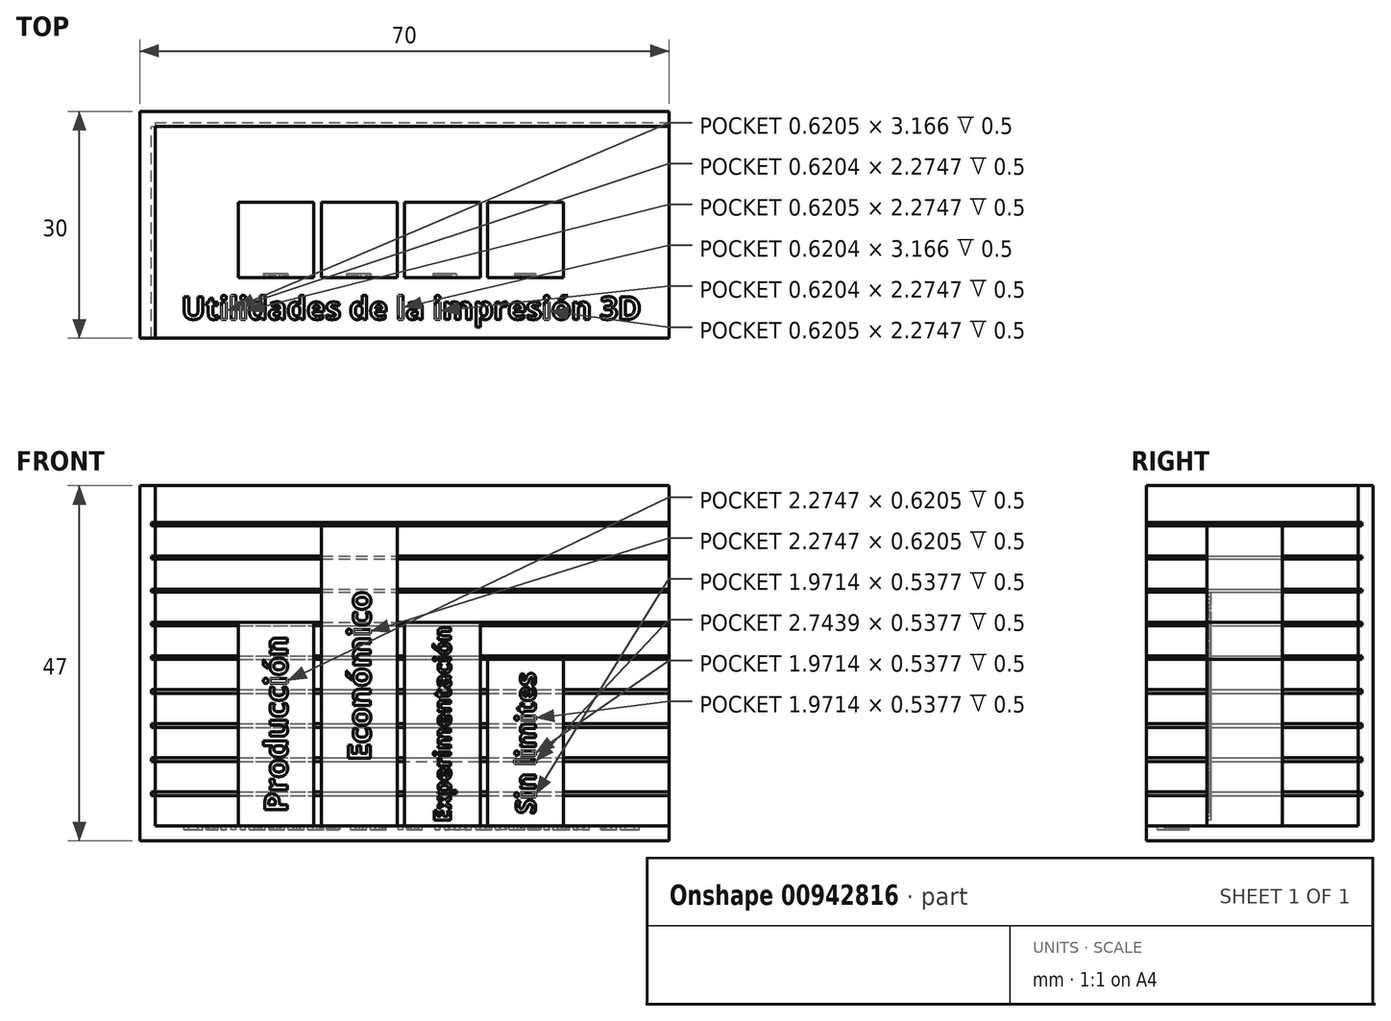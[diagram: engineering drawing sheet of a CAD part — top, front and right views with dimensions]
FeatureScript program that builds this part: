
annotation { "Feature Type Name" : "Feature", "Feature Type Description" : "" }
export const myFeature = defineFeature(function(context is Context, id is Id, definition is map)
    precondition{}
    {
        {
            var Q0;
            Q0=qCreatedBy(makeId("Top.planeOp"),FACE);
            var sketch = newSketch(context, id + "F0", { "sketchPlane" : qUnion([Q0])});
            skLineSegment(sketch, "E0.bottom", {"start": v(-35, 15) * mm, "end": v(35, 15) * mm});
            skLineSegment(sketch, "E0.top", {"start": v(-35, -15) * mm, "end": v(35, -15) * mm});
            skLineSegment(sketch, "E0.left", {"start": v(-35, 15) * mm, "end": v(-35, -15) * mm});
            skLineSegment(sketch, "E0.right", {"start": v(35, 15) * mm, "end": v(35, -15) * mm});
            skPoint(sketch, "E0.middle", {"position": v(0, 0) * mm});
            skSolve(sketch);
        }
        {
            var Q0;
            Q0 = qSketchRegion(id + "F0", true);
            extrude(context, id + "F1", {"entities" : qUnion([Q0]), "depth" : 2 * mm, "offsetDistance" : 25 * mm});
        }
        {
            var Q0;
            Q0=makeQuery(id+"F1.opExtrude","SWEPT_FACE",FACE,{"disambiguationData":[OSD([sQuery(id+"F0.wireOp",EDGE,"E0.bottom")])]});
            cPlane(context, id + "F2", {"entities" : qUnion([Q0]), "cplaneType" : CPlaneType.OFFSET, "offset" : 0 * mm, "width" : 150 * mm, "height" : 150 * mm});
        }
        {
            var Q0;
            Q0=makeQuery(id+"F1.opExtrude","SWEPT_FACE",FACE,{"disambiguationData":[OSD([sQuery(id+"F0.wireOp",EDGE,"E0.left")])]});
            cPlane(context, id + "F3", {"entities" : qUnion([Q0]), "cplaneType" : CPlaneType.OFFSET, "offset" : 0 * mm, "width" : 150 * mm, "height" : 150 * mm});
        }
        {
            var Q0;
            Q0=qCreatedBy(id+"F3.planeOp",FACE);
            var sketch = newSketch(context, id + "F4", { "sketchPlane" : qUnion([Q0])});
            skLineSegment(sketch, "E1.bottom", {"start": v(-15, 2) * mm, "end": v(15, 2) * mm});
            skLineSegment(sketch, "E1.top", {"start": v(-15, 47) * mm, "end": v(15, 47) * mm});
            skLineSegment(sketch, "E1.left", {"start": v(-15, 2) * mm, "end": v(-15, 47) * mm});
            skLineSegment(sketch, "E1.right", {"start": v(15, 2) * mm, "end": v(15, 47) * mm});
            skSolve(sketch);
        }
        {
            var Q0;
            Q0=qCreatedBy(id+"F2.planeOp",FACE);
            var sketch = newSketch(context, id + "F5", { "sketchPlane" : qUnion([Q0])});
            skLineSegment(sketch, "E2.bottom", {"start": v(35, 2) * mm, "end": v(-35, 2) * mm});
            skLineSegment(sketch, "E2.top", {"start": v(35, 47) * mm, "end": v(-35, 47) * mm});
            skLineSegment(sketch, "E2.left", {"start": v(35, 2) * mm, "end": v(35, 47) * mm});
            skLineSegment(sketch, "E2.right", {"start": v(-35, 2) * mm, "end": v(-35, 47) * mm});
            skSolve(sketch);
        }
        {
            var Q0;
            Q0 = qSketchRegion(id + "F4", true);
            extrude(context, id + "F6", {"entities" : qUnion([Q0]), "oppositeDirection" : true, "depth" : 2 * mm, "offsetDistance" : 25 * mm});
        }
        {
            var Q0;
            Q0 = qSketchRegion(id + "F5", true);
            extrude(context, id + "F7", {"entities" : qUnion([Q0]), "operationType" : NewBodyOperationType.ADD, "oppositeDirection" : true, "depth" : 2 * mm, "offsetDistance" : 25 * mm});
        }
        {
            var Q0;
            Q0=makeQuery(id+"F6.opExtrude","CAP_FACE",FACE,{"disambiguationData":[OSD([sQuery(id+"F4.wireOp",EDGE,"E1.bottom"),sQuery(id+"F4.wireOp",EDGE,"E1.top"),sQuery(id+"F4.wireOp",EDGE,"E1.left"),sQuery(id+"F4.wireOp",EDGE,"E1.right")])],"isStart":false});
            var sketch = newSketch(context, id + "F8", { "sketchPlane" : qUnion([Q0])});
            skLineSegment(sketch, "E3.bottom", {"start": v(-15, 6.5) * mm, "end": v(13, 6.5) * mm});
            skLineSegment(sketch, "E3.top", {"start": v(-15, 6) * mm, "end": v(13, 6) * mm});
            skLineSegment(sketch, "E3.left", {"start": v(-15, 6.5) * mm, "end": v(-15, 6) * mm});
            skLineSegment(sketch, "E3.right", {"start": v(13, 6.5) * mm, "end": v(13, 6) * mm});
            skLineSegment(sketch, "E4.bottom", {"start": v(-15, 11) * mm, "end": v(13, 11) * mm});
            skLineSegment(sketch, "E4.top", {"start": v(-15, 10.5) * mm, "end": v(13, 10.5) * mm});
            skLineSegment(sketch, "E4.left", {"start": v(-15, 11) * mm, "end": v(-15, 10.5) * mm});
            skLineSegment(sketch, "E4.right", {"start": v(13, 11) * mm, "end": v(13, 10.5) * mm});
            skLineSegment(sketch, "E5.bottom", {"start": v(-15, 15.5) * mm, "end": v(13, 15.5) * mm});
            skLineSegment(sketch, "E5.top", {"start": v(-15, 15) * mm, "end": v(13, 15) * mm});
            skLineSegment(sketch, "E5.left", {"start": v(-15, 15.5) * mm, "end": v(-15, 15) * mm});
            skLineSegment(sketch, "E5.right", {"start": v(13, 15.5) * mm, "end": v(13, 15) * mm});
            skLineSegment(sketch, "E6.bottom", {"start": v(-15, 20) * mm, "end": v(13, 20) * mm});
            skLineSegment(sketch, "E6.top", {"start": v(-15, 19.5) * mm, "end": v(13, 19.5) * mm});
            skLineSegment(sketch, "E6.left", {"start": v(-15, 20) * mm, "end": v(-15, 19.5) * mm});
            skLineSegment(sketch, "E6.right", {"start": v(13, 20) * mm, "end": v(13, 19.5) * mm});
            skLineSegment(sketch, "E7.bottom", {"start": v(-15, 24.5) * mm, "end": v(13, 24.5) * mm});
            skLineSegment(sketch, "E7.top", {"start": v(-15, 24) * mm, "end": v(13, 24) * mm});
            skLineSegment(sketch, "E7.left", {"start": v(-15, 24.5) * mm, "end": v(-15, 24) * mm});
            skLineSegment(sketch, "E7.right", {"start": v(13, 24.5) * mm, "end": v(13, 24) * mm});
            skLineSegment(sketch, "E8.bottom", {"start": v(-15, 28.9) * mm, "end": v(13, 28.9) * mm});
            skLineSegment(sketch, "E8.top", {"start": v(-15, 28.5) * mm, "end": v(13, 28.5) * mm});
            skLineSegment(sketch, "E8.left", {"start": v(-15, 28.9) * mm, "end": v(-15, 28.5) * mm});
            skLineSegment(sketch, "E8.right", {"start": v(13, 28.9) * mm, "end": v(13, 28.5) * mm});
            skLineSegment(sketch, "E9.bottom", {"start": v(-15, 33.3) * mm, "end": v(13, 33.3) * mm});
            skLineSegment(sketch, "E9.top", {"start": v(-15, 32.9) * mm, "end": v(13, 32.9) * mm});
            skLineSegment(sketch, "E9.left", {"start": v(-15, 33.3) * mm, "end": v(-15, 32.9) * mm});
            skLineSegment(sketch, "E9.right", {"start": v(13, 33.3) * mm, "end": v(13, 32.9) * mm});
            skLineSegment(sketch, "E10.bottom", {"start": v(-15, 37.7) * mm, "end": v(13, 37.7) * mm});
            skLineSegment(sketch, "E10.top", {"start": v(-15, 37.3) * mm, "end": v(13, 37.3) * mm});
            skLineSegment(sketch, "E10.left", {"start": v(-15, 37.7) * mm, "end": v(-15, 37.3) * mm});
            skLineSegment(sketch, "E10.right", {"start": v(13, 37.7) * mm, "end": v(13, 37.3) * mm});
            skLineSegment(sketch, "E11.bottom", {"start": v(-15, 42.1) * mm, "end": v(13, 42.1) * mm});
            skLineSegment(sketch, "E11.top", {"start": v(-15, 41.7) * mm, "end": v(13, 41.7) * mm});
            skLineSegment(sketch, "E11.left", {"start": v(-15, 42.1) * mm, "end": v(-15, 41.7) * mm});
            skLineSegment(sketch, "E11.right", {"start": v(13, 42.1) * mm, "end": v(13, 41.7) * mm});
            skSolve(sketch);
        }
        {
            var Q0;
            Q0 = qSketchRegion(id + "F8", true);
            extrude(context, id + "F9", {"entities" : qUnion([Q0]), "operationType" : NewBodyOperationType.REMOVE, "oppositeDirection" : true, "depth" : 0.5 * mm, "offsetDistance" : 25 * mm});
        }
        {
            var Q0;
            Q0=makeQuery(id+"F9.boolean.opBoolean","MERGE",FACE,{"derivedFrom":[makeQuery(id+"F7.opExtrude","CAP_FACE",FACE,{"disambiguationData":[OSD([sQuery(id+"F5.wireOp",EDGE,"E2.bottom"),sQuery(id+"F5.wireOp",EDGE,"E2.top"),sQuery(id+"F5.wireOp",EDGE,"E2.left"),sQuery(id+"F5.wireOp",EDGE,"E2.right")])],"isStart":false})],"fromTools":[makeQuery(id+"F9.opExtrude","SWEPT_FACE",FACE,{"disambiguationData":[OSD([sQuery(id+"F8.wireOp",EDGE,"E3.right")])]}),makeQuery(id+"F9.opExtrude","SWEPT_FACE",FACE,{"disambiguationData":[OSD([sQuery(id+"F8.wireOp",EDGE,"E4.right")])]}),makeQuery(id+"F9.opExtrude","SWEPT_FACE",FACE,{"disambiguationData":[OSD([sQuery(id+"F8.wireOp",EDGE,"E5.right")])]}),makeQuery(id+"F9.opExtrude","SWEPT_FACE",FACE,{"disambiguationData":[OSD([sQuery(id+"F8.wireOp",EDGE,"E6.right")])]}),makeQuery(id+"F9.opExtrude","SWEPT_FACE",FACE,{"disambiguationData":[OSD([sQuery(id+"F8.wireOp",EDGE,"E7.right")])]}),makeQuery(id+"F9.opExtrude","SWEPT_FACE",FACE,{"disambiguationData":[OSD([sQuery(id+"F8.wireOp",EDGE,"E8.right")])]}),makeQuery(id+"F9.opExtrude","SWEPT_FACE",FACE,{"disambiguationData":[OSD([sQuery(id+"F8.wireOp",EDGE,"E9.right")])]}),makeQuery(id+"F9.opExtrude","SWEPT_FACE",FACE,{"disambiguationData":[OSD([sQuery(id+"F8.wireOp",EDGE,"E10.right")])]}),makeQuery(id+"F9.opExtrude","SWEPT_FACE",FACE,{"disambiguationData":[OSD([sQuery(id+"F8.wireOp",EDGE,"E11.right")])]})]});
            var sketch = newSketch(context, id + "F10", { "sketchPlane" : qUnion([Q0])});
            skLineSegment(sketch, "E12.bottom", {"start": v(-33, 6.5) * mm, "end": v(35, 6.5) * mm});
            skLineSegment(sketch, "E12.top", {"start": v(-33, 6) * mm, "end": v(35, 6) * mm});
            skLineSegment(sketch, "E12.left", {"start": v(-33, 6.5) * mm, "end": v(-33, 6) * mm});
            skLineSegment(sketch, "E12.right", {"start": v(35, 6.5) * mm, "end": v(35, 6) * mm});
            skLineSegment(sketch, "E13.bottom", {"start": v(-33, 11) * mm, "end": v(35, 11) * mm});
            skLineSegment(sketch, "E13.top", {"start": v(-33, 10.5) * mm, "end": v(35, 10.5) * mm});
            skLineSegment(sketch, "E13.left", {"start": v(-33, 11) * mm, "end": v(-33, 10.5) * mm});
            skLineSegment(sketch, "E13.right", {"start": v(35, 11) * mm, "end": v(35, 10.5) * mm});
            skLineSegment(sketch, "E14.bottom", {"start": v(-33, 15.5) * mm, "end": v(35, 15.5) * mm});
            skLineSegment(sketch, "E14.top", {"start": v(-33, 15) * mm, "end": v(35, 15) * mm});
            skLineSegment(sketch, "E14.left", {"start": v(-33, 15.5) * mm, "end": v(-33, 15) * mm});
            skLineSegment(sketch, "E14.right", {"start": v(35, 15.5) * mm, "end": v(35, 15) * mm});
            skLineSegment(sketch, "E15.bottom", {"start": v(-33, 20) * mm, "end": v(35, 20) * mm});
            skLineSegment(sketch, "E15.top", {"start": v(-33, 19.5) * mm, "end": v(35, 19.5) * mm});
            skLineSegment(sketch, "E15.left", {"start": v(-33, 20) * mm, "end": v(-33, 19.5) * mm});
            skLineSegment(sketch, "E15.right", {"start": v(35, 20) * mm, "end": v(35, 19.5) * mm});
            skLineSegment(sketch, "E16.bottom", {"start": v(-33, 24.5) * mm, "end": v(35, 24.5) * mm});
            skLineSegment(sketch, "E16.top", {"start": v(-33, 24) * mm, "end": v(35, 24) * mm});
            skLineSegment(sketch, "E16.left", {"start": v(-33, 24.5) * mm, "end": v(-33, 24) * mm});
            skLineSegment(sketch, "E16.right", {"start": v(35, 24.5) * mm, "end": v(35, 24) * mm});
            skLineSegment(sketch, "E17.bottom", {"start": v(-33, 28.9) * mm, "end": v(35, 28.9) * mm});
            skLineSegment(sketch, "E17.top", {"start": v(-33, 28.5) * mm, "end": v(35, 28.5) * mm});
            skLineSegment(sketch, "E17.left", {"start": v(-33, 28.9) * mm, "end": v(-33, 28.5) * mm});
            skLineSegment(sketch, "E17.right", {"start": v(35, 28.9) * mm, "end": v(35, 28.5) * mm});
            skLineSegment(sketch, "E18.bottom", {"start": v(-33, 33.3) * mm, "end": v(35, 33.3) * mm});
            skLineSegment(sketch, "E18.top", {"start": v(-33, 32.9) * mm, "end": v(35, 32.9) * mm});
            skLineSegment(sketch, "E18.left", {"start": v(-33, 33.3) * mm, "end": v(-33, 32.9) * mm});
            skLineSegment(sketch, "E18.right", {"start": v(35, 33.3) * mm, "end": v(35, 32.9) * mm});
            skLineSegment(sketch, "E19.bottom", {"start": v(-33, 37.7) * mm, "end": v(35, 37.7) * mm});
            skLineSegment(sketch, "E19.top", {"start": v(-33, 37.3) * mm, "end": v(35, 37.3) * mm});
            skLineSegment(sketch, "E19.left", {"start": v(-33, 37.7) * mm, "end": v(-33, 37.3) * mm});
            skLineSegment(sketch, "E19.right", {"start": v(35, 37.7) * mm, "end": v(35, 37.3) * mm});
            skLineSegment(sketch, "E20.bottom", {"start": v(-33, 42.1) * mm, "end": v(35, 42.1) * mm});
            skLineSegment(sketch, "E20.top", {"start": v(-33, 41.7) * mm, "end": v(35, 41.7) * mm});
            skLineSegment(sketch, "E20.left", {"start": v(-33, 42.1) * mm, "end": v(-33, 41.7) * mm});
            skLineSegment(sketch, "E20.right", {"start": v(35, 42.1) * mm, "end": v(35, 41.7) * mm});
            skSolve(sketch);
        }
        {
            var Q0;
            Q0=makeQuery(id+"F1.opExtrude","CAP_FACE",FACE,{"disambiguationData":[OSD([sQuery(id+"F0.wireOp",EDGE,"E0.bottom"),sQuery(id+"F0.wireOp",EDGE,"E0.top"),sQuery(id+"F0.wireOp",EDGE,"E0.left"),sQuery(id+"F0.wireOp",EDGE,"E0.right")])],"isStart":false});
            var sketch = newSketch(context, id + "F11", { "sketchPlane" : qUnion([Q0])});
            skLineSegment(sketch, "E21.bottom", {"start": v(-22, 3) * mm, "end": v(-12, 3) * mm});
            skLineSegment(sketch, "E21.top", {"start": v(-22, -7) * mm, "end": v(-12, -7) * mm});
            skLineSegment(sketch, "E21.left", {"start": v(-22, 3) * mm, "end": v(-22, -7) * mm});
            skLineSegment(sketch, "E21.right", {"start": v(-12, 3) * mm, "end": v(-12, -7) * mm});
            skLineSegment(sketch, "E22.bottom", {"start": v(-11, 3) * mm, "end": v(-1, 3) * mm});
            skLineSegment(sketch, "E22.top", {"start": v(-11, -7) * mm, "end": v(-1, -7) * mm});
            skLineSegment(sketch, "E22.left", {"start": v(-11, 3) * mm, "end": v(-11, -7) * mm});
            skLineSegment(sketch, "E22.right", {"start": v(-1, 3) * mm, "end": v(-1, -7) * mm});
            skLineSegment(sketch, "E23.bottom", {"start": v(0, 3) * mm, "end": v(10, 3) * mm});
            skLineSegment(sketch, "E23.top", {"start": v(0, -7) * mm, "end": v(10, -7) * mm});
            skLineSegment(sketch, "E23.left", {"start": v(0, 3) * mm, "end": v(0, -7) * mm});
            skLineSegment(sketch, "E23.right", {"start": v(10, 3) * mm, "end": v(10, -7) * mm});
            skLineSegment(sketch, "E24.bottom", {"start": v(11, -7) * mm, "end": v(21, -7) * mm});
            skLineSegment(sketch, "E24.top", {"start": v(11, 3) * mm, "end": v(21, 3) * mm});
            skLineSegment(sketch, "E24.left", {"start": v(11, -7) * mm, "end": v(11, 3) * mm});
            skLineSegment(sketch, "E24.right", {"start": v(21, -7) * mm, "end": v(21, 3) * mm});
            skSolve(sketch);
        }
        {
            var Q0;
            Q0=makeQuery(id+"F11.imprint","IMPRINT",FACE,{"disambiguationData":[TD([[makeQuery(id+"F11.imprint","IMPRINT",EDGE,{"derivedFrom":sQuery(id+"F11.wireOp",EDGE,"E21.bottom")}),-1.0]])]});
            extrude(context, id + "F12", {"entities" : qUnion([Q0]), "operationType" : NewBodyOperationType.ADD, "depth" : 26.9 * mm, "offsetDistance" : 25 * mm});
        }
        {
            var Q0;
            Q0=makeQuery(id+"F11.imprint","IMPRINT",FACE,{"disambiguationData":[TD([[makeQuery(id+"F11.imprint","IMPRINT",EDGE,{"derivedFrom":sQuery(id+"F11.wireOp",EDGE,"E22.bottom")}),-1.0]])]});
            extrude(context, id + "F13", {"entities" : qUnion([Q0]), "operationType" : NewBodyOperationType.ADD, "depth" : 39.7 * mm, "offsetDistance" : 25 * mm});
        }
        {
            var Q0;
            Q0=makeQuery(id+"F11.imprint","IMPRINT",FACE,{"disambiguationData":[TD([[makeQuery(id+"F11.imprint","IMPRINT",EDGE,{"derivedFrom":sQuery(id+"F11.wireOp",EDGE,"E23.bottom")}),-1.0]])]});
            extrude(context, id + "F14", {"entities" : qUnion([Q0]), "operationType" : NewBodyOperationType.ADD, "depth" : 26.9 * mm, "offsetDistance" : 25 * mm});
        }
        {
            var Q0;
            Q0=makeQuery(id+"F11.imprint","IMPRINT",FACE,{"disambiguationData":[TD([[makeQuery(id+"F11.imprint","IMPRINT",EDGE,{"derivedFrom":sQuery(id+"F11.wireOp",EDGE,"E24.bottom")}),1.0]])]});
            extrude(context, id + "F15", {"entities" : qUnion([Q0]), "operationType" : NewBodyOperationType.ADD, "depth" : 22 * mm, "offsetDistance" : 25 * mm});
        }
        {
            var Q0;
            Q0 = qSketchRegion(id + "F10", true);
            extrude(context, id + "F16", {"entities" : qUnion([Q0]), "operationType" : NewBodyOperationType.REMOVE, "oppositeDirection" : true, "depth" : 0.5 * mm, "offsetDistance" : 25 * mm});
        }
        {
            var Q0;
            Q0=makeQuery(id+"F1.opExtrude","CAP_FACE",FACE,{"disambiguationData":[OSD([sQuery(id+"F0.wireOp",EDGE,"E0.bottom"),sQuery(id+"F0.wireOp",EDGE,"E0.top"),sQuery(id+"F0.wireOp",EDGE,"E0.left"),sQuery(id+"F0.wireOp",EDGE,"E0.right")])],"isStart":false});
            var sketch = newSketch(context, id + "F17", { "sketchPlane" : qUnion([Q0])});
            skText(sketch, "E25", { "text": "Utilidades de la impresión 3D\n", "fontName": "OpenSans-Bold.ttf"});
            const initialGuessF17  = {"E25": [-0.0295, -0.01251, 1, 0, 0.003]};
            skSetInitialGuess(sketch, initialGuessF17);
            skSolve(sketch);
        }
        {
            var Q0;
            Q0 = qSketchRegion(id + "F17", true);
            extrude(context, id + "F18", {"entities" : qUnion([Q0]), "operationType" : NewBodyOperationType.REMOVE, "oppositeDirection" : true, "depth" : 0.5 * mm, "offsetDistance" : 25 * mm});
        }
        {
            var Q0;
            Q0=makeQuery(id+"F12.opExtrude","SWEPT_FACE",FACE,{"disambiguationData":[OSD([sQuery(id+"F11.wireOp",EDGE,"E21.top")])]});
            var sketch = newSketch(context, id + "F19", { "sketchPlane" : qUnion([Q0])});
            skText(sketch, "E26", { "text": "Producción", "fontName": "OpenSans-Bold.ttf"});
            skLineSegment(sketch, "E27", {"start": v(-17, 3.8) * mm, "end": v(-17, 27.1) * mm, "construction": true});
            skLineSegment(sketch, "E28", {"start": v(-15.5, 15.45) * mm, "end": v(-18.5, 15.45) * mm, "construction": true});
            const initialGuessF19  = {"E26": [-0.0155, 0.0038, 0, 1, 0.003]};
            skSetInitialGuess(sketch, initialGuessF19);
            skSolve(sketch);
        }
        {
            var Q0;
            Q0 = qSketchRegion(id + "F19", true);
            extrude(context, id + "F20", {"entities" : qUnion([Q0]), "operationType" : NewBodyOperationType.REMOVE, "oppositeDirection" : true, "depth" : 0.5 * mm, "offsetDistance" : 25 * mm});
        }
        {
            var Q0;
            Q0=makeQuery(id+"F13.opExtrude","SWEPT_FACE",FACE,{"disambiguationData":[OSD([sQuery(id+"F11.wireOp",EDGE,"E22.top")])]});
            var sketch = newSketch(context, id + "F21", { "sketchPlane" : qUnion([Q0])});
            skText(sketch, "E29", { "text": "Económico", "fontName": "OpenSans-Bold.ttf"});
            skLineSegment(sketch, "E30", {"start": v(-6, 10.58) * mm, "end": v(-6, 33.12) * mm, "construction": true});
            skLineSegment(sketch, "E31", {"start": v(-7.5, 21.85) * mm, "end": v(-4.5, 21.85) * mm, "construction": true});
            const initialGuessF21  = {"E29": [-0.0045, 0.01058, 0, 1, 0.003]};
            skSetInitialGuess(sketch, initialGuessF21);
            skSolve(sketch);
        }
        {
            var Q0;
            Q0 = qSketchRegion(id + "F21", true);
            extrude(context, id + "F22", {"entities" : qUnion([Q0]), "operationType" : NewBodyOperationType.REMOVE, "oppositeDirection" : true, "depth" : 0.5 * mm, "offsetDistance" : 25 * mm});
        }
        {
            var Q0;
            Q0=makeQuery(id+"F14.opExtrude","SWEPT_FACE",FACE,{"disambiguationData":[OSD([sQuery(id+"F11.wireOp",EDGE,"E23.top")])]});
            var sketch = newSketch(context, id + "F23", { "sketchPlane" : qUnion([Q0])});
            skText(sketch, "E32", { "text": "Experimentación", "fontName": "OpenSans-Bold.ttf"});
            skLineSegment(sketch, "E33", {"start": v(5, 2.5) * mm, "end": v(5, 28.4) * mm, "construction": true});
            skText(sketch, "E34", { "text": "Sin limites", "fontName": "OpenSans-Bold.ttf"});
            skLineSegment(sketch, "E35", {"start": v(16, 3.56) * mm, "end": v(16, 22.44) * mm, "construction": true});
            const initialGuessF23  = {"E32": [0.0061, 0.0025, 0, 1, 0.0022], "E34": [0.0173, 0.00356, 0, 1, 0.0026]};
            skSetInitialGuess(sketch, initialGuessF23);
            skSolve(sketch);
        }
        {
            var Q0;
            Q0 = qSketchRegion(id + "F23", true);
            extrude(context, id + "F24", {"entities" : qUnion([Q0]), "operationType" : NewBodyOperationType.REMOVE, "oppositeDirection" : true, "depth" : 0.5 * mm, "offsetDistance" : 25 * mm});
        }
    });
